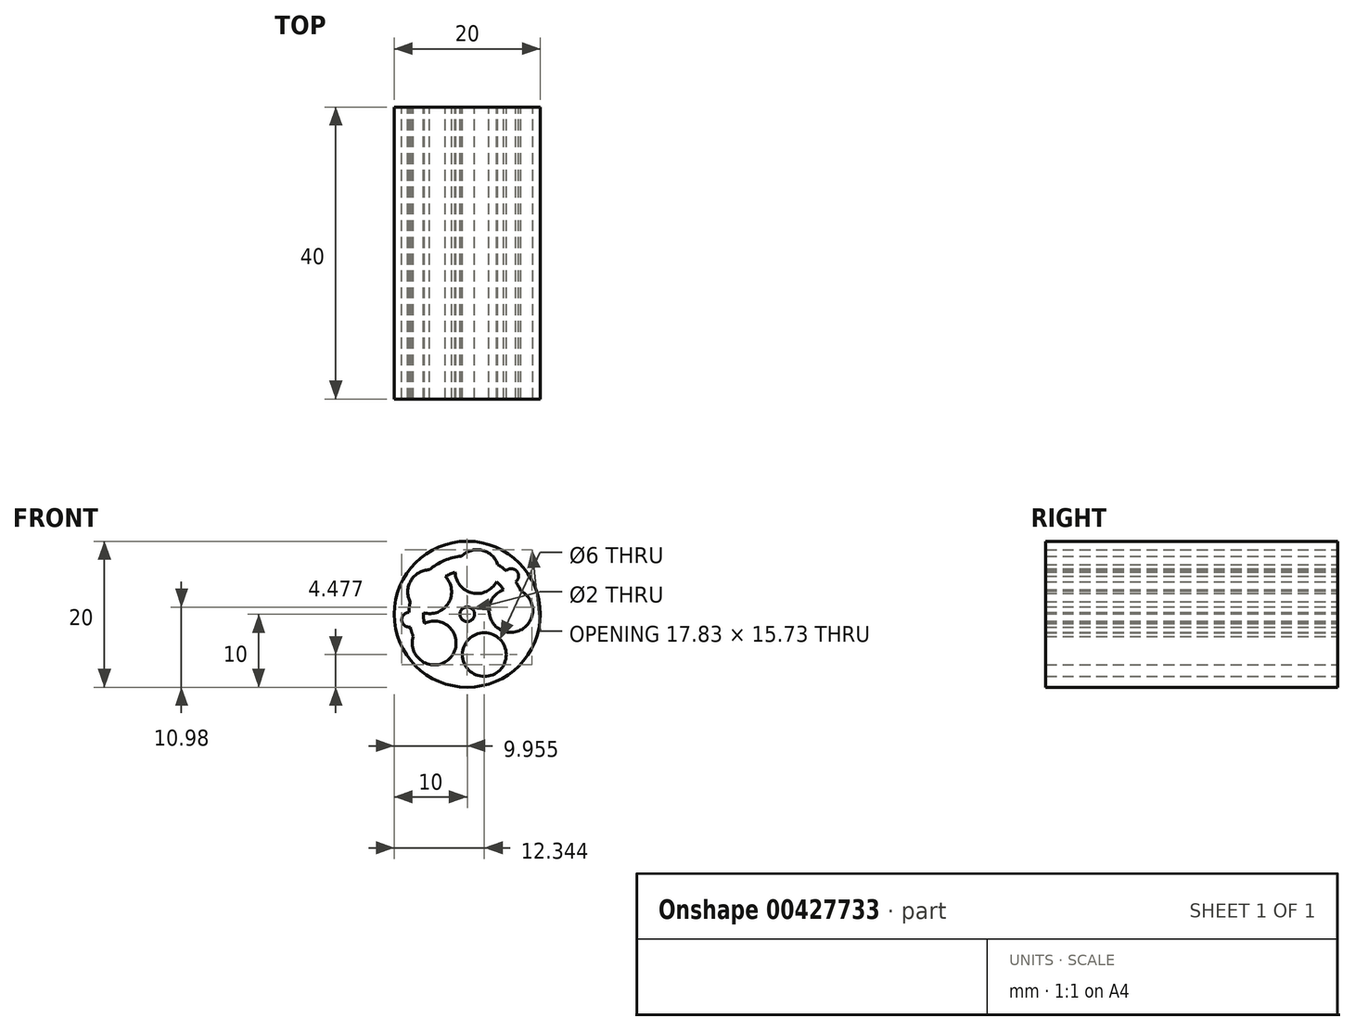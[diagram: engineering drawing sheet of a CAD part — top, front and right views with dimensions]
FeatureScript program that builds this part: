
annotation { "Feature Type Name" : "Feature", "Feature Type Description" : "" }
export const myFeature = defineFeature(function(context is Context, id is Id, definition is map)
    precondition{}
    {
        {
            var Q0;
            Q0=qCreatedBy(makeId("Front.planeOp"),FACE);
            var sketch = newSketch(context, id + "F0", { "sketchPlane" : qUnion([Q0])});
            skCircle(sketch, "E0", {"center": v(0, 0) * mm, "radius": 10 * mm});
            skCircle(sketch, "E1", {"center": v(0, 0) * mm, "radius": 1 * mm});
            skCircle(sketch, "E2", {"center": v(0, 0) * mm, "radius": 3 * mm});
            skCircle(sketch, "E3", {"center": v(1.35, 5.85) * mm, "radius": 3 * mm});
            skCircle(sketch, "E4", {"center": v(5.98, 0.52) * mm, "radius": 3 * mm});
            skCircle(sketch, "E5", {"center": v(2.34, -5.52) * mm, "radius": 3 * mm});
            skCircle(sketch, "E6", {"center": v(-4.53, -3.94) * mm, "radius": 3 * mm});
            skCircle(sketch, "E7", {"center": v(-5.14, 3.1) * mm, "radius": 3 * mm});
            skLineSegment(sketch, "E8", {"start": v(-4.53, -3.94) * mm, "end": v(2.34, -5.52) * mm});
            skCircle(sketch, "E9", {"center": v(0, 0) * mm, "radius": 6 * mm});
            skCircle(sketch, "E10", {"center": v(0, 0) * mm, "radius": 8 * mm});
            skCircle(sketch, "E11", {"center": v(-7.96, -0.75) * mm, "radius": 1 * mm});
            skCircle(sketch, "E12", {"center": v(6.04, 5.25) * mm, "radius": 1 * mm});
            skSolve(sketch);
        }
        {
            var Q0;
            Q0=makeQuery(id+"F0.imprint","IMPRINT",FACE,{"disambiguationData":[TD([[makeQuery(id+"F0.imprint","IMPRINT",EDGE,{"derivedFrom":sQuery(id+"F0.wireOp",EDGE,"E0")}),1.0]])]});
            var Q1;
            {var subQ0=sQuery(id+"F0.wireOp",EDGE,"E3");var subQ1=sQuery(id+"F0.wireOp",EDGE,"E2");var subQ2=makeQuery(id+"F0.imprint","INTERSECT",VERTEX,{"derivedFrom":[subQ1,subQ0]});Q1=makeQuery(id+"F0.imprint","IMPRINT",FACE,{"disambiguationData":[TD([[makeQuery(id+"F0.imprint","IMPRINT",EDGE,{"disambiguationData":[TD([[subQ2,-1.0]])],"derivedFrom":subQ1}),-1.0]])]});}
            var Q2;
            {var subQ0=sQuery(id+"F0.wireOp",EDGE,"E3");var subQ1=sQuery(id+"F0.wireOp",EDGE,"E2");var subQ2=makeQuery(id+"F0.imprint","INTERSECT",VERTEX,{"derivedFrom":[subQ1,subQ0]});Q2=makeQuery(id+"F0.imprint","IMPRINT",FACE,{"disambiguationData":[TD([[makeQuery(id+"F0.imprint","IMPRINT",EDGE,{"disambiguationData":[TD([[subQ2,1.0]])],"derivedFrom":subQ1}),-1.0]])]});}
            var Q3;
            {var subQ0=sQuery(id+"F0.wireOp",EDGE,"E4");var subQ1=sQuery(id+"F0.wireOp",EDGE,"E2");var subQ2=makeQuery(id+"F0.imprint","INTERSECT",VERTEX,{"derivedFrom":[subQ1,subQ0]});Q3=makeQuery(id+"F0.imprint","IMPRINT",FACE,{"disambiguationData":[TD([[makeQuery(id+"F0.imprint","IMPRINT",EDGE,{"disambiguationData":[TD([[subQ2,1.0]])],"derivedFrom":subQ1}),-1.0]])]});}
            var Q4;
            {var subQ0=sQuery(id+"F0.wireOp",EDGE,"E6");var subQ1=sQuery(id+"F0.wireOp",EDGE,"E2");var subQ2=makeQuery(id+"F0.imprint","INTERSECT",VERTEX,{"derivedFrom":[subQ1,subQ0]});Q4=makeQuery(id+"F0.imprint","IMPRINT",FACE,{"disambiguationData":[TD([[makeQuery(id+"F0.imprint","IMPRINT",EDGE,{"disambiguationData":[TD([[subQ2,-1.0]])],"derivedFrom":subQ1}),-1.0]])]});}
            var Q5;
            {var subQ0=sQuery(id+"F0.wireOp",EDGE,"E8");var subQ1=sQuery(id+"F0.wireOp",EDGE,"E5");var subQ2=makeQuery(id+"F0.imprint","INTERSECT",VERTEX,{"derivedFrom":[subQ1,subQ0]});Q5=makeQuery(id+"F0.imprint","IMPRINT",FACE,{"disambiguationData":[TD([[makeQuery(id+"F0.imprint","IMPRINT",EDGE,{"disambiguationData":[TD([[subQ2,-1.0]])],"derivedFrom":subQ1}),-1.0]])]});}
            var Q6;
            {var subQ0=sQuery(id+"F0.wireOp",EDGE,"E9");var subQ1=sQuery(id+"F0.wireOp",EDGE,"E5");var subQ2=makeQuery(id+"F0.imprint","INTERSECT",VERTEX,{"disambiguationData":[OD(1.0)],"derivedFrom":[subQ1,subQ0]});Q6=makeQuery(id+"F0.imprint","IMPRINT",FACE,{"disambiguationData":[TD([[makeQuery(id+"F0.imprint","IMPRINT",EDGE,{"disambiguationData":[TD([[subQ2,-1.0]])],"derivedFrom":subQ1}),-1.0]])]});}
            var Q7;
            {var subQ0=sQuery(id+"F0.wireOp",EDGE,"E7");var subQ1=sQuery(id+"F0.wireOp",EDGE,"E2");var subQ2=makeQuery(id+"F0.imprint","INTERSECT",VERTEX,{"derivedFrom":[subQ1,subQ0]});Q7=makeQuery(id+"F0.imprint","IMPRINT",FACE,{"disambiguationData":[TD([[makeQuery(id+"F0.imprint","IMPRINT",EDGE,{"disambiguationData":[TD([[subQ2,-1.0]])],"derivedFrom":subQ1}),-1.0]])]});}
            var Q8;
            {var subQ5=sQuery(id+"F0.wireOp",EDGE,"E9");var subQ6=sQuery(id+"F0.wireOp",EDGE,"E6");var subQ7=makeQuery(id+"F0.imprint","INTERSECT",VERTEX,{"disambiguationData":[OD(0.0)],"derivedFrom":[subQ6,subQ5]});Q8=makeQuery(id+"F0.imprint","IMPRINT",FACE,{"disambiguationData":[TD([[makeQuery(id+"F0.imprint","IMPRINT",EDGE,{"disambiguationData":[TD([[subQ7,-1.0]])],"derivedFrom":subQ6}),-1.0]])]});}
            var Q9;
            {var subQ0=sQuery(id+"F0.wireOp",EDGE,"E9");var subQ1=sQuery(id+"F0.wireOp",EDGE,"E4");var subQ2=makeQuery(id+"F0.imprint","INTERSECT",VERTEX,{"disambiguationData":[OD(1.0)],"derivedFrom":[subQ1,subQ0]});Q9=makeQuery(id+"F0.imprint","IMPRINT",FACE,{"disambiguationData":[TD([[makeQuery(id+"F0.imprint","IMPRINT",EDGE,{"disambiguationData":[TD([[subQ2,-1.0]])],"derivedFrom":subQ1}),-1.0]])]});}
            var Q10;
            {var subQ0=sQuery(id+"F0.wireOp",EDGE,"E10");var subQ6=sQuery(id+"F0.wireOp",EDGE,"E3");var subQ9=makeQuery(id+"F0.imprint","INTERSECT",VERTEX,{"disambiguationData":[OD(1.0)],"derivedFrom":[subQ6,subQ0]});Q10=makeQuery(id+"F0.imprint","IMPRINT",FACE,{"disambiguationData":[TD([[makeQuery(id+"F0.imprint","IMPRINT",EDGE,{"disambiguationData":[TD([[subQ9,1.0]])],"derivedFrom":subQ6}),-1.0]])]});}
            var Q11;
            Q11=makeQuery(id+"F0.imprint","IMPRINT",FACE,{"disambiguationData":[TD([[makeQuery(id+"F0.imprint","IMPRINT",EDGE,{"derivedFrom":sQuery(id+"F0.wireOp",EDGE,"E1")}),-1.0]])]});
            var Q12;
            {var subQ0=sQuery(id+"F0.wireOp",EDGE,"E10");var subQ1=sQuery(id+"F0.wireOp",EDGE,"E3");var subQ2=makeQuery(id+"F0.imprint","INTERSECT",VERTEX,{"disambiguationData":[OD(0.0)],"derivedFrom":[subQ1,subQ0]});Q12=makeQuery(id+"F0.imprint","IMPRINT",FACE,{"disambiguationData":[TD([[makeQuery(id+"F0.imprint","IMPRINT",EDGE,{"disambiguationData":[TD([[subQ2,-1.0]])],"derivedFrom":subQ1}),-1.0]])]});}
            extrude(context, id + "F1", {"entities" : qUnion([Q0, Q1, Q2, Q3, Q4, Q5, Q6, Q7, Q8, Q9, Q10, Q11, Q12]), "depth" : 40 * mm, "offsetDistance" : 25 * mm});
        }
    });
